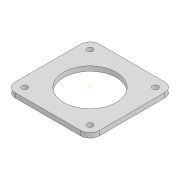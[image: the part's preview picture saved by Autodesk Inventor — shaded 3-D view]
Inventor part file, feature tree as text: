
AUTODESK INVENTOR PART (.ipt)
format: ipt  version: 2020 (Build 240168000, 168)  size: 116,224 bytes
history: native  units: mm
features: mirror x2, sketch x2, other x1, extrude x1
ambient origin geometry x8: Origin, YZ Plane, XZ Plane, XY Plane, X Axis, Y Axis, Z Axis, Center Point
bodies: Body1 (feature_tree)
feature tree (6):
  other  "Sólido1"
  extrude  "Extrusão1"  Depth=36.0mm
  mirror  "Espelhamento1"
  mirror  "Espelhamento2"
  sketch  "Esboço2"  dims[d2=36.0mm d3=8.0mm d4=5.0mm d5=4.0mm d6=0.0mm d7=8.0mm d8=8.0mm]
  sketch  "Esboço1"  dims[d0=45.0mm d1=36.0mm]
